# Revit family: Toilet-Bidet-American_Standard-Advanced_Clean-297AA204.291
name_source: partatom
category: Plumbing Fixtures
revit_build: Autodesk Revit 2014 (Build: 20130308_1515(x64)
units: mm (PartAtom-declared; Revit-internal decimal feet)

## types (1)
- 297AA204.291
    ADA Compliant = Yes
    Assembly Code = D2010100
    Bowl Shape = Elongated
    CW Connection = Yes
    CWFU = 5
    Cold Water Connection Diameter = 1/2"
    Cold Water Connection Height = 5 15/16"
    Cold Water Connection Radius = 1/4"
    Cold Water Connection Width = 11"
    Default Elevation = 0"
    Description = Advanced Clean® 100 SpaLet® Toilet
    Electrical Connection Height = 12 1/2"
    Electrical Connection Width = 11"
    Finish = Vitreous China-American Standard-291 Alabaster White
    Flush Rate = Dual Flush 0.92 - 1.32 gpf (3.4 - 4.9 Lpf)
    Frequency = 60 Hz
    HW Connection = Yes
    HWFU = 0
    Height = 20 5/8"
    Hot Water Connection Diameter = 1"
    Hot Water Connection Radius = 1/4"
    Installation Type = Floor Mounted
    Length = 25 1/16"
    Manufacturer = American Standard
    Material = Vitreous China-American Standard-291 Alabaster White
    Model = 297AA204.291
    Price = Prices may vary. Please consult Manufacturer Representative for most up-to-date price list.
    Seat Specification = 8017A60GRC.291 Advanced Clean 100 Seat
    Tempered Water Connection Diameter = 1/2"
    Tempered Water Connection Radius = 1/4"
    URL = http://www.americanstandard-us.com
    Vent Connection = No
    Voltage = 120 V
    WFU = 5
    Warranty Documentation Link = https://www.americanstandard-us.com
    Waste Connection = Yes
    Waste Connection Diameter = 2 9/16"
    Waste Connection Radius = 1 9/32"
    Width = 14 3/4"

## geometry (parser evidence)
native form markers: Sweep x1
no freeform markers — native parametric forms only
